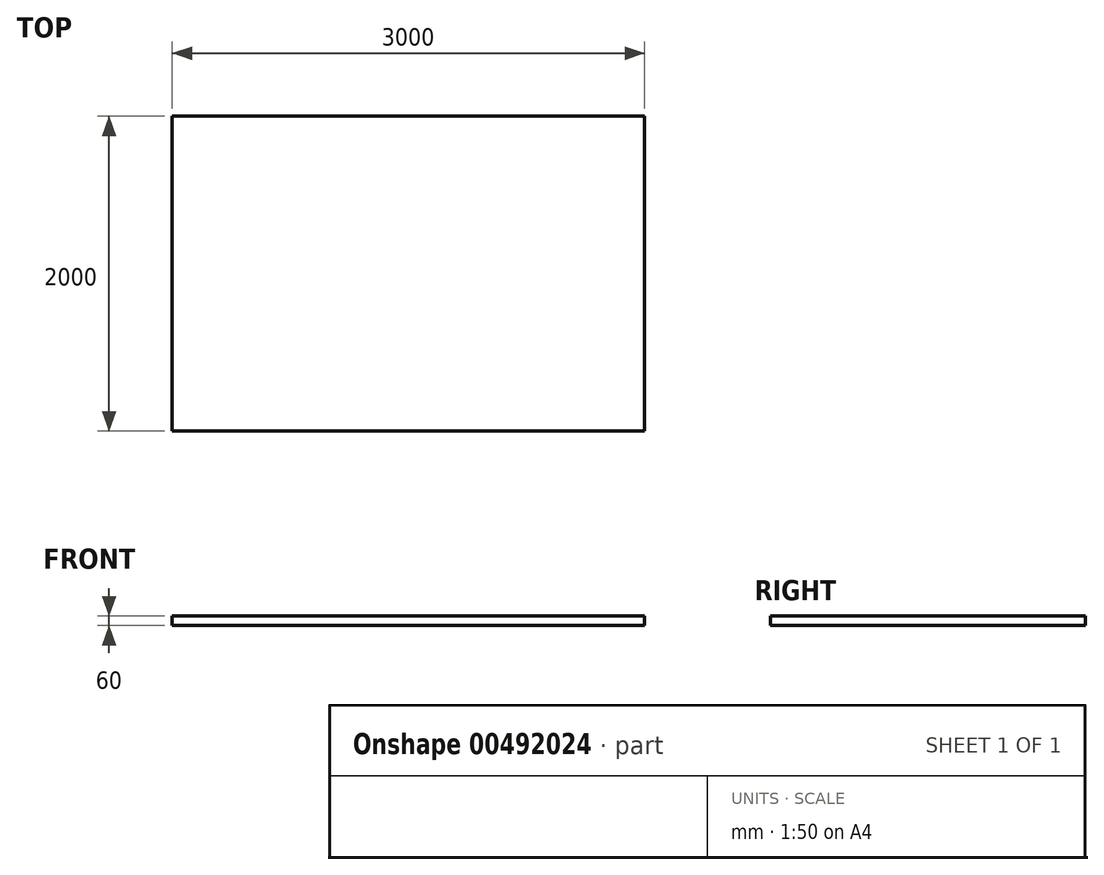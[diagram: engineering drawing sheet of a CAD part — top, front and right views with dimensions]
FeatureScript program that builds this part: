
annotation { "Feature Type Name" : "Feature", "Feature Type Description" : "" }
export const myFeature = defineFeature(function(context is Context, id is Id, definition is map)
    precondition{}
    {
        {
            var Q0;
            Q0=qCreatedBy(makeId("Top.planeOp"),FACE);
            var sketch = newSketch(context, id + "F0", { "sketchPlane" : qUnion([Q0])});
            skLineSegment(sketch, "E0.bottom", {"start": v(-1500, 1000) * mm, "end": v(1500, 1000) * mm});
            skLineSegment(sketch, "E0.top", {"start": v(-1500, -1000) * mm, "end": v(1500, -1000) * mm});
            skLineSegment(sketch, "E0.left", {"start": v(-1500, 1000) * mm, "end": v(-1500, -1000) * mm});
            skLineSegment(sketch, "E0.right", {"start": v(1500, 1000) * mm, "end": v(1500, -1000) * mm});
            skSolve(sketch);
        }
        {
            var Q0;
            Q0 = qSketchRegion(id + "F0", true);
            extrude(context, id + "F1", {"entities" : qUnion([Q0]), "depth" : 60 * mm});
        }
    });
